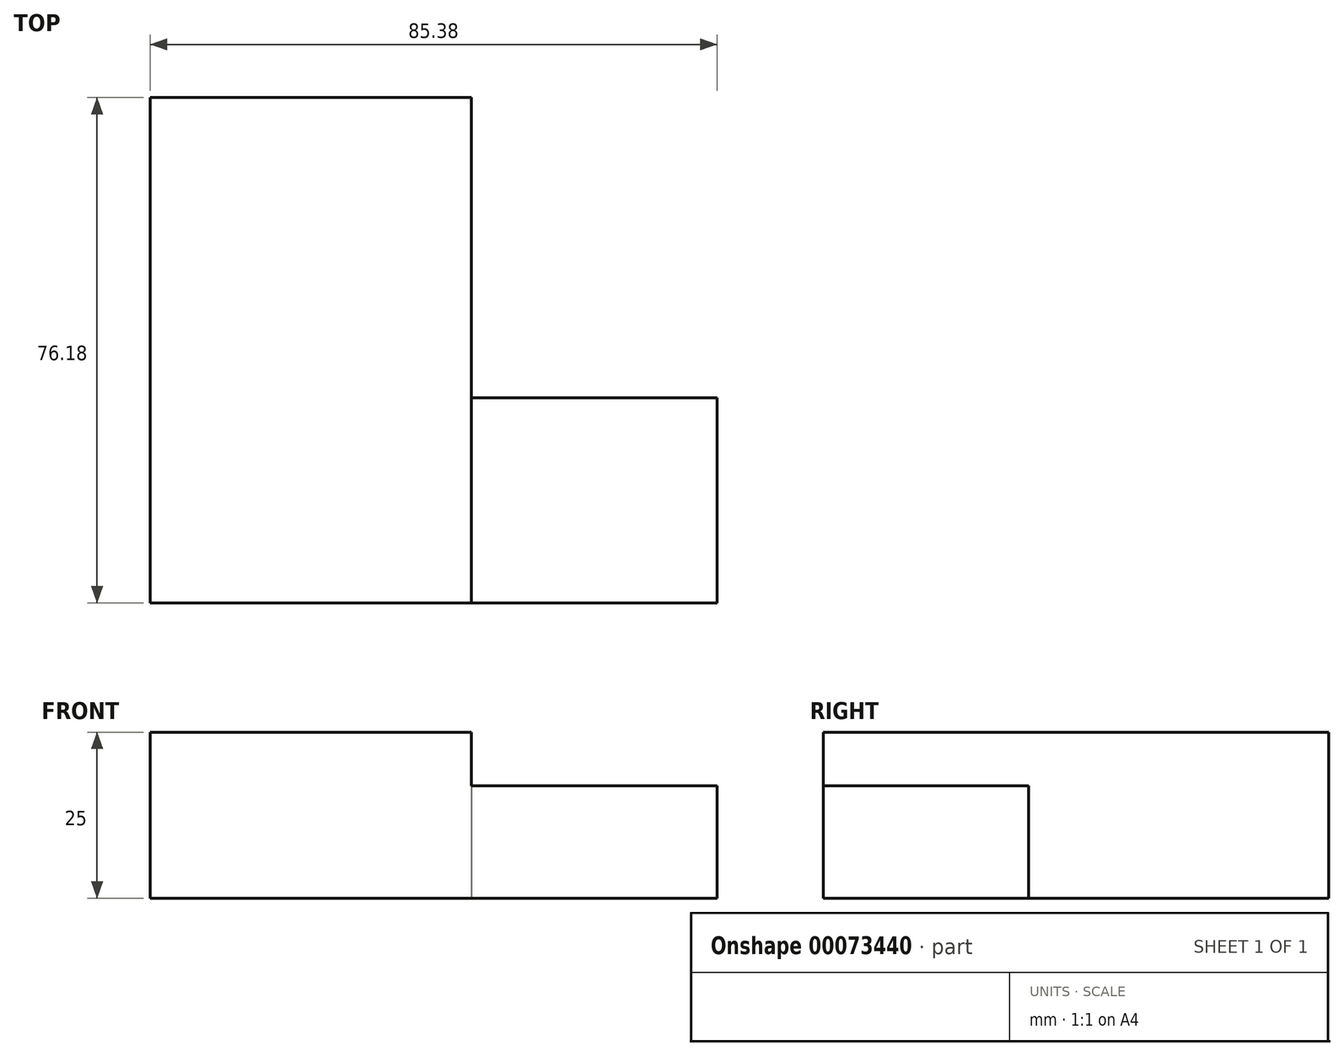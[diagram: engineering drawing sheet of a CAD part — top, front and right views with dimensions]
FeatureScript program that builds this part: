
annotation { "Feature Type Name" : "Feature", "Feature Type Description" : "" }
export const myFeature = defineFeature(function(context is Context, id is Id, definition is map)
    precondition{}
    {
        {
            var Q0;
            Q0=qCreatedBy(makeId("Top.planeOp"),FACE);
            var sketch = newSketch(context, id + "F0", { "sketchPlane" : qUnion([Q0])});
            skLineSegment(sketch, "E0.bottom", {"start": v(-30.26, 38.61) * mm, "end": v(18.15, 38.61) * mm});
            skLineSegment(sketch, "E0.top", {"start": v(-30.26, -37.57) * mm, "end": v(18.15, -37.57) * mm});
            skLineSegment(sketch, "E0.left", {"start": v(-30.26, 38.61) * mm, "end": v(-30.26, -37.57) * mm});
            skLineSegment(sketch, "E0.right", {"start": v(18.15, 38.61) * mm, "end": v(18.15, -37.57) * mm});
            skLineSegment(sketch, "E1.bottom", {"start": v(55.12, -6.65) * mm, "end": v(18.15, -6.65) * mm});
            skLineSegment(sketch, "E1.top", {"start": v(55.12, -37.57) * mm, "end": v(18.15, -37.57) * mm});
            skLineSegment(sketch, "E1.left", {"start": v(55.12, -6.65) * mm, "end": v(55.12, -37.57) * mm});
            skLineSegment(sketch, "E1.right", {"start": v(18.15, -6.65) * mm, "end": v(18.15, -37.57) * mm});
            skSolve(sketch);
        }
        {
            var Q0;
            Q0=makeQuery(id+"F0.imprint","IMPRINT",FACE,{"disambiguationData":[TD([[makeQuery(id+"F0.imprint","IMPRINT",EDGE,{"derivedFrom":sQuery(id+"F0.wireOp",EDGE,"E0.bottom")}),-1.0]])]});
            extrude(context, id + "F4", {"entities" : qUnion([Q0]), "depth" : 25 * mm});
        }
        {
            var Q0;
            Q0=makeQuery(id+"F0.imprint","IMPRINT",FACE,{"disambiguationData":[TD([[makeQuery(id+"F0.imprint","IMPRINT",EDGE,{"derivedFrom":sQuery(id+"F0.wireOp",EDGE,"E1.bottom")}),1.0]])]});
            extrude(context, id + "F1", {"entities" : qUnion([Q0]), "operationType" : NewBodyOperationType.ADD, "depth" : 16.95 * mm});
        }
        {
            var Q0;
            Q0=makeQuery(id+"F4.opExtrude","CAP_VERTEX",VERTEX,{"disambiguationData":[OSD([sQuery(id+"F0.wireOp",EDGE,"E0.bottom"),sQuery(id+"F0.wireOp",EDGE,"E0.left")])],"isStart":false});
            var Q1;
            Q1=makeQuery(id+"F1.opExtrude","CAP_VERTEX",VERTEX,{"disambiguationData":[OSD([sQuery(id+"F0.wireOp",EDGE,"E1.top"),sQuery(id+"F0.wireOp",EDGE,"E1.left")])],"isStart":false});
            var Q2;
            Q2=sQuery(id+"F0.wireOp",VERTEX,"E1.left.end");
            cPlane(context, id + "F2", {"entities" : qUnion([Q0, Q1, Q2]), "cplaneType" : CPlaneType.THREE_POINT, "offset" : 150 * mm, "width" : 150 * mm, "height" : 150 * mm});
        }
    });
